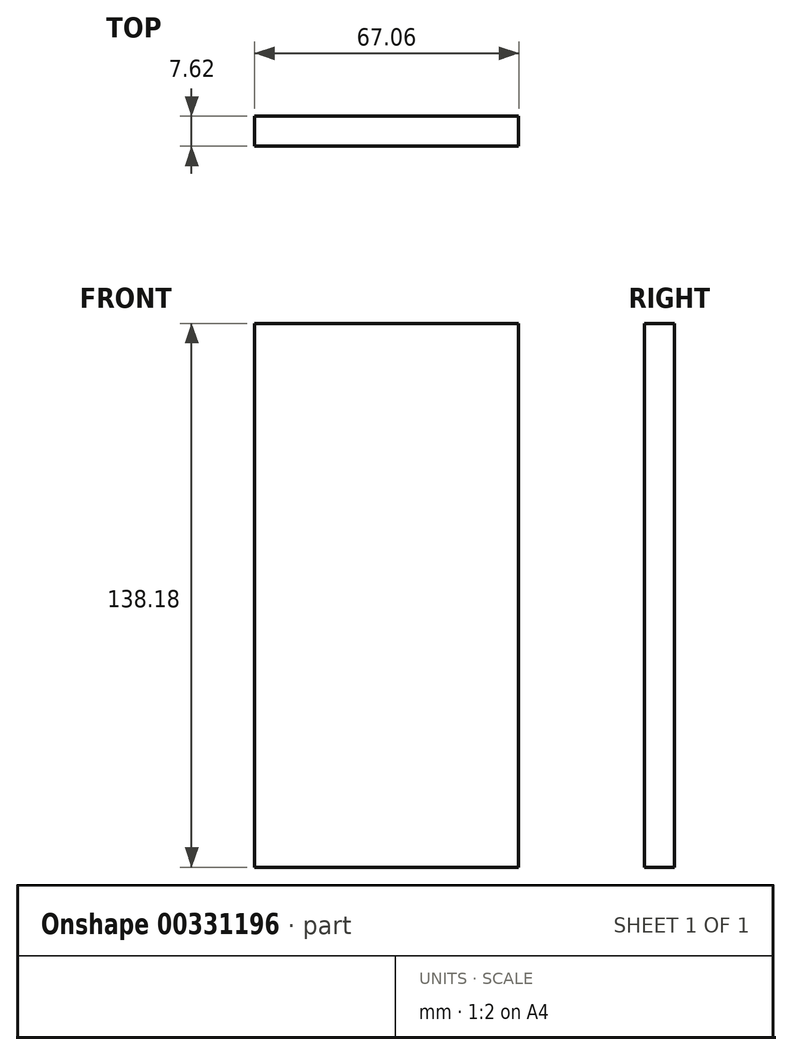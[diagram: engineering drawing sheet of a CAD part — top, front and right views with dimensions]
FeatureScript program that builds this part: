
annotation { "Feature Type Name" : "Feature", "Feature Type Description" : "" }
export const myFeature = defineFeature(function(context is Context, id is Id, definition is map)
    precondition{}
    {
        {
            var Q0;
            Q0=qCreatedBy(makeId("Front.planeOp"),FACE);
            var sketch = newSketch(context, id + "F0", { "sketchPlane" : qUnion([Q0])});
            skLineSegment(sketch, "E0.bottom", {"start": v(-33.53, -69.09) * mm, "end": v(33.53, -69.09) * mm});
            skLineSegment(sketch, "E0.top", {"start": v(-33.53, 69.09) * mm, "end": v(33.53, 69.09) * mm});
            skLineSegment(sketch, "E0.left", {"start": v(-33.53, -69.09) * mm, "end": v(-33.53, 69.09) * mm});
            skLineSegment(sketch, "E0.right", {"start": v(33.53, -69.09) * mm, "end": v(33.53, 69.09) * mm});
            skPoint(sketch, "E0.middle", {"position": v(0, 0) * mm});
            skSolve(sketch);
        }
        {
            var Q0;
            Q0=makeQuery(id+"F0.imprint","IMPRINT",FACE,{"disambiguationData":[TD([[makeQuery(id+"F0.imprint","IMPRINT",EDGE,{"derivedFrom":sQuery(id+"F0.wireOp",EDGE,"E0.bottom")}),1.0]])]});
            extrude(context, id + "F1", {"entities" : qUnion([Q0]), "depth" : 7.62 * mm});
        }
    });
